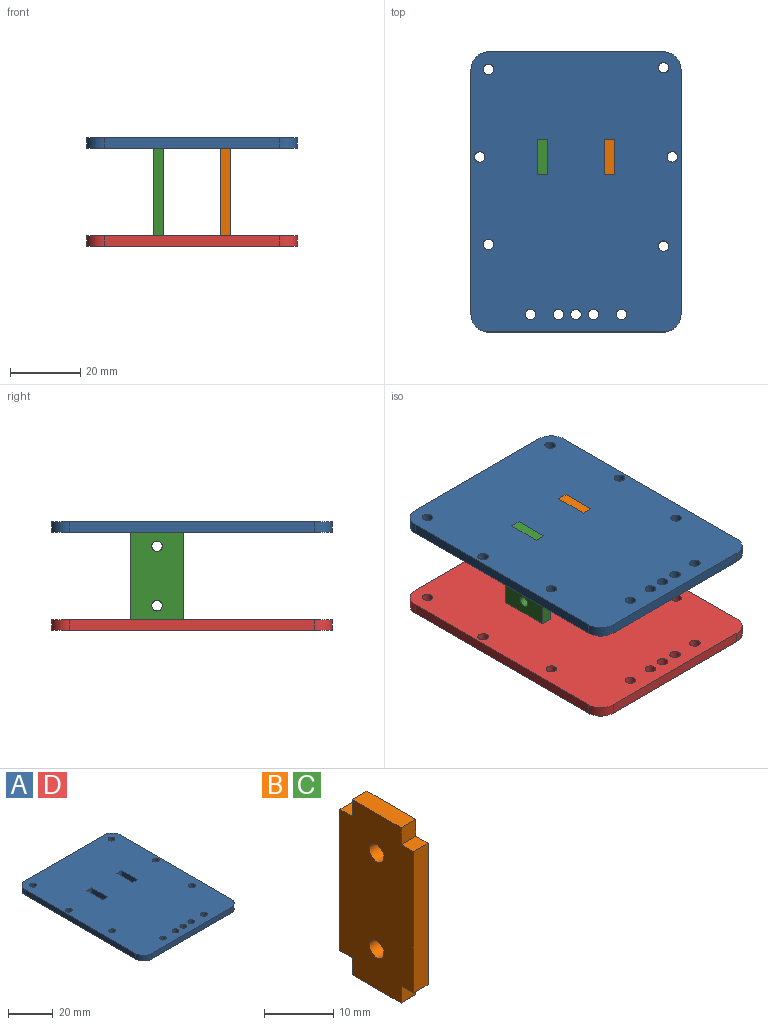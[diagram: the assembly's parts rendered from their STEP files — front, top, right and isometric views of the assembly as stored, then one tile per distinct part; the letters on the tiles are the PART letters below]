
ASSEMBLY  parts=4 mates=3
PART A: 29 faces, bbox 60x80x3 mm
  f0: plane 70x3mm, normal (-1,0,0), area 210mm2, adj f1,f15,f27,f28
  f1: cylinder r=5mm len=5mm, axis (0,0,1), area 23.6mm2, adj f0,f2,f27,f28
  f2: plane 50x3mm, normal (0,-1,0), area 150mm2, adj f1,f3,f27,f28
  f3: cylinder r=5mm len=5mm, axis (0,0,1), area 23.6mm2, adj f2,f4,f27,f28
  f4: plane 70x3mm, normal (1,0,0), area 210mm2, adj f3,f5,f27,f28
  f5: cylinder r=5mm len=5mm, axis (0,0,1), area 23.6mm2, adj f4,f6,f27,f28
  f6: plane 50x3mm, normal (0,1,0), area 150mm2, adj f5,f15,f27,f28
  f7: plane 10x3mm, normal (-1,0,0), area 30mm2, adj f8,f14,f27,f28
  f8: plane 3x3mm, normal (0,1,0), area 9mm2, adj f7,f9,f27,f28
  f9: plane 10x3mm, normal (1,0,0), area 30mm2, adj f8,f14,f27,f28
  f10: plane 10x3mm, normal (-1,0,0), area 30mm2, adj f11,f13,f27,f28
  f11: plane 3x3mm, normal (0,1,0), area 9mm2, adj f10,f12,f27,f28
  f12: plane 10x3mm, normal (1,0,0), area 30mm2, adj f11,f13,f27,f28
  f13: plane 3x3mm, normal (0,-1,0), area 9mm2, adj f10,f12,f27,f28
  f14: plane 3x3mm, normal (0,-1,0), area 9mm2, adj f7,f9,f27,f28
  f15: cylinder r=5mm len=5mm, axis (0,0,1), area 23.6mm2, adj f0,f6,f27,f28
  f16: cylinder r=1.5mm len=3mm, axis (0,0,1), area 28.3mm2, adj f27,f28
  f17: cylinder r=1.5mm len=3mm, axis (0,0,1), area 28.3mm2, adj f27,f28
  f18: cylinder r=1.5mm len=3mm, axis (0,0,1), area 28.3mm2, adj f27,f28
  f19: cylinder r=1.5mm len=3mm, axis (0,0,1), area 28.3mm2, adj f27,f28
  f20: cylinder r=1.5mm len=3mm, axis (0,0,1), area 28.3mm2, adj f27,f28
  f21: cylinder r=1.5mm len=3mm, axis (0,0,1), area 28.3mm2, adj f27,f28
  f22: cylinder r=1.5mm len=3mm, axis (0,0,1), area 28.3mm2, adj f27,f28
  f23: cylinder r=1.5mm len=3mm, axis (0,0,1), area 28.3mm2, adj f27,f28
  f24: cylinder r=1.5mm len=3mm, axis (0,0,1), area 28.3mm2, adj f27,f28
  f25: cylinder r=1.5mm len=3mm, axis (0,0,1), area 28.3mm2, adj f27,f28
  f26: cylinder r=1.5mm len=3mm, axis (0,0,1), area 28.3mm2, adj f27,f28
  f27: plane 80x60mm, normal (0,0,1), area 4640.8mm2, adj f0,f1,f2,f3,f4,f5,f6,f7
  f28: plane 80x60mm, normal (0,0,-1), area 4640.8mm2, adj f0,f1,f2,f3,f4,f5,f6,f7
PART B: 16 faces, bbox 3x15x31 mm
  f0: plane 3x3mm, normal (0,-1,0), area 9mm2, adj f1,f13,f14,f15
  f1: plane 10x3mm, normal (0,0,-1), area 30mm2, adj f0,f2,f14,f15
  f2: plane 3x3mm, normal (0,1,0), area 9mm2, adj f1,f3,f14,f15
  f3: plane 3x2.5mm, normal (0,0,-1), area 7.5mm2, adj f2,f4,f14,f15
  f4: plane 25x3mm, normal (0,1,0), area 75mm2, adj f3,f5,f14,f15
  f5: plane 3x2.5mm, normal (0,0,1), area 7.5mm2, adj f4,f6,f14,f15
  f6: plane 3x3mm, normal (0,1,0), area 9mm2, adj f5,f7,f14,f15
  f7: plane 10x3mm, normal (0,0,1), area 30mm2, adj f6,f8,f14,f15
  f8: plane 3x3mm, normal (0,-1,0), area 9mm2, adj f7,f9,f14,f15
  f9: plane 3x2.5mm, normal (0,0,1), area 7.5mm2, adj f8,f10,f14,f15
  f10: plane 25x3mm, normal (0,-1,0), area 75mm2, adj f9,f13,f14,f15
  f11: cylinder r=1.5mm len=3mm, axis (1,0,0), area 28.3mm2, adj f14,f15
  f12: cylinder r=1.5mm len=3mm, axis (1,0,0), area 28.3mm2, adj f14,f15
  f13: plane 3x2.5mm, normal (0,0,-1), area 7.5mm2, adj f0,f10,f14,f15
  f14: plane 31x15mm, normal (1,0,0), area 420.9mm2, adj f0,f1,f2,f3,f4,f5,f6,f7
  f15: plane 31x15mm, normal (-1,0,0), area 420.9mm2, adj f0,f1,f2,f3,f4,f5,f6,f7
PART C: same geometry as B
PART D: same geometry as A
PLACE A t=(-16.5,-19.2,39.76)mm
PLACE B t=(-8.5,-26.7,14.76)mm
PLACE C t=(-27.5,-26.7,14.76)mm
PLACE D t=(-16.5,-19.2,11.76)mm
MATE fastened D.f11 <-> C.f0  axis (0,1,0) through (-26,-24.2,13.26)mm
MATE fastened B.f8 <-> A.f8  axis (0,-1,0) through (-7,-24.2,41.26)mm
MATE fastened B.f0 <-> D.f8  axis (0,-1,0) through (-7,-24.2,13.26)mm
